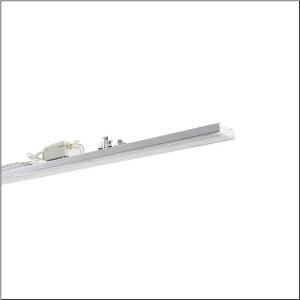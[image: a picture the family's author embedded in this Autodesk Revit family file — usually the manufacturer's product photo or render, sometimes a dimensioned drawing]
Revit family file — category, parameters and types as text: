
# Revit family: licross_21_recessed_mo_52tl1ede445g
name_source: partatom
category: Lighting Fixtures
units: mm (PartAtom-declared; Revit-internal decimal feet)

## family parameters
Cut with Voids When Loaded = No
Host = Face
Light Source = No
Part Type = Normal
Room Calculation Point = No
Round Connector Dimension = Use Diameter
Shared = No

## types (1)
- --- (1 x LED, 4970 lm, 29.9 W, 4000K)
    Apparent Load = 30 VA
    CIE Flux Codes = 85 95 99 100 100
    Color Rendering = 80
    Color Temperature = 4000K
    Default Elevation = 1800 mm
    Description = Licross 21 Recessed MO, luminaire insert, of sheet steel, galvanised, coil coated, white, length: 750mm, width: 66mm, height: 67mm, LED rated luminous flux: 4.970lm, light colour: 840, SDCM (Standard Deviation of Colour Matching)MacAdam ≤ 3 SDCM (initial), control gear: DALI 2, with plug, 5-pole, with phase selection, mains connection: 220..240V, AC, 50/60Hz, rated input power: 30W, internal wiring halogen-free, primary light control with lens, of plastic, primary optical cover: cover, of PMMA, light emission: direct distribution, primary light characteristic: symmetric, protection rating (complete): IP40, insulation class (complete): insulation class I (protective earthing), certification: CE, ENEC, VDE, UKCA, protection symbol: D if used in an environment without relevant dust loads with corresponding accessories, impact resistance: IK06, permissible ambient temperature for indoor applications: -25..+35°C, corresponds to IFS (International Featured Standards) requirements for safety and quality in the food industry, reducing of maximum allowable ambient temperature of 5°C with ceiling mounting, LABS conformity tested according to VDMA 24364:2018-05, The light source and the operating device comply with the requirements of the Ecodesign Regulation (EU) 2019/2020 and are replaceable in accordance with this regulation, packaging unit: 1 piece
    Height = 58 mm
    Lamp = 1 x LED
    Lamp Light Flux = 4970 lm
    Lamp Power = 29.9 W
    Lamp count = 1
    Length = 750 mm
    Luminous efficacy = 166 lm/W
    Manufacturer = Siteco
    ModVariant = No
    Model = 52TL1EDE445G
    Mounting Place = Ceiling
    Mounting Type = Pendant
    Number of Poles = 1
    OnlyDefault = Yes
    Power Factor = 1
    Product Name = Licross 21 Recessed MO
    Product group = luminaire insert | ceiling pendant
    ProductGroupID = 901
    Protection Class = Protection class I
    Protection Degree = IP 40
    RLX_Detail_Level = 1
    RLX_Emergency_Light_Flux = 0 lm
    RLX_Emergency_Type = 0
    RLX_Emergency_Type_DB = No
    RlxData = <blob elided: 29249 chars, md5=e0f4cfe1>
    Socket = socket
    Standby Power = 0 W
    System Light Flux = 4970 lm
    System Power = 30 W
    Type Comments = factory setting: luminous flux: 100 % | dim-lin: 254 | 390 mA
    Type Image = l_1296930.jpg
    URL = http://relux.com
    VarID = @adj_127397
    Voltage = 0 V
    Weight = 0.00 kg
    Width = 66 mm

## geometry (parser evidence)
native form markers: Blend x4, Sweep x8
no freeform markers — native parametric forms only
